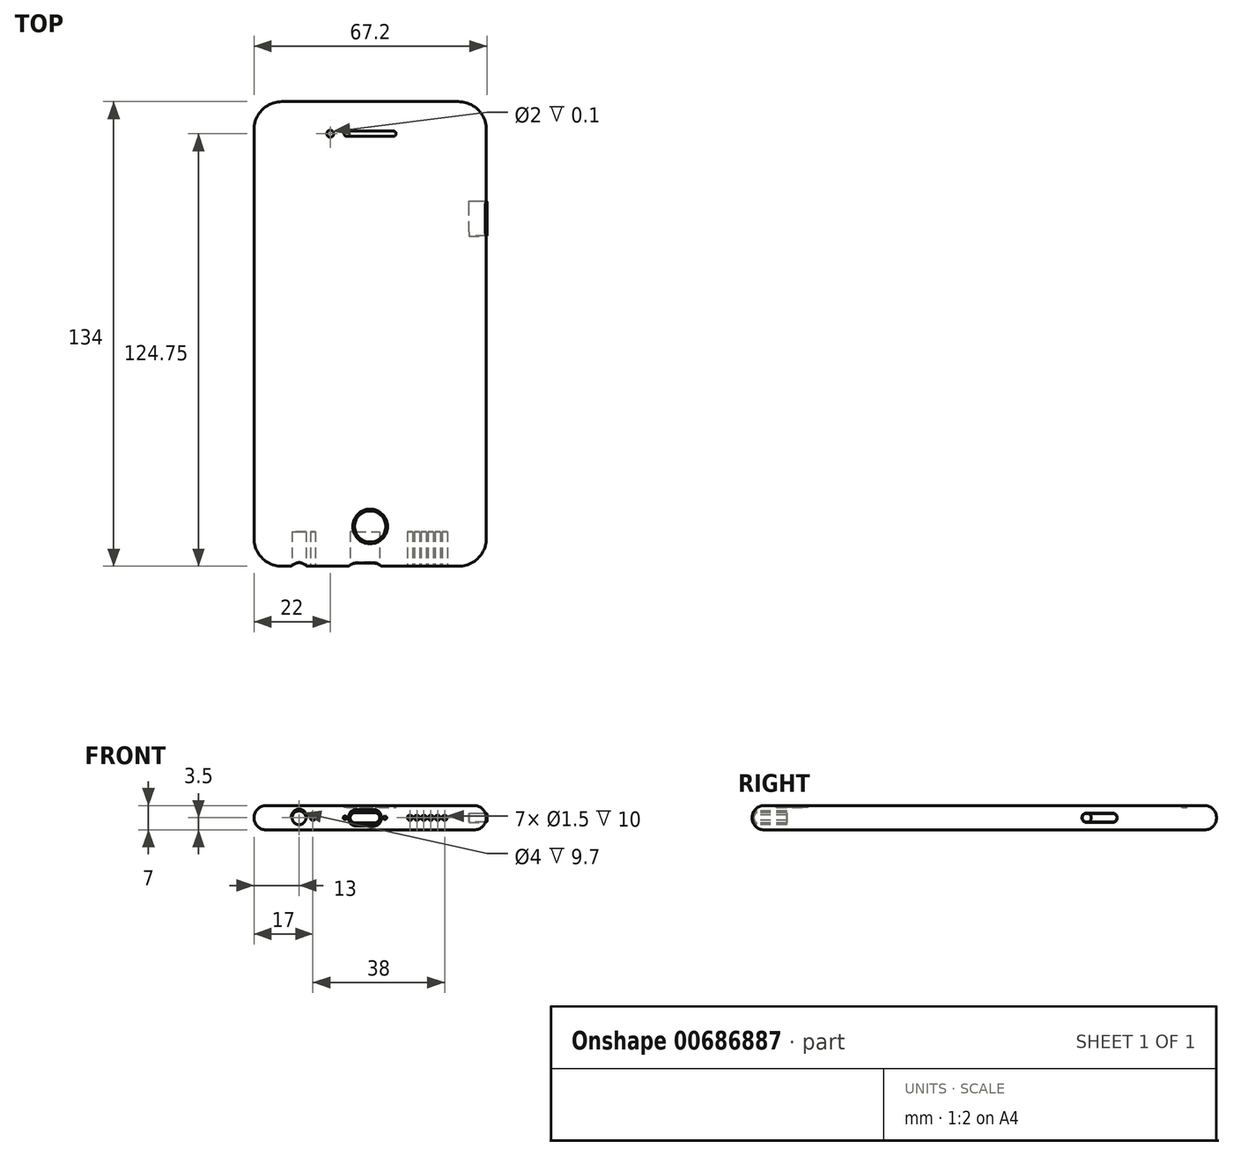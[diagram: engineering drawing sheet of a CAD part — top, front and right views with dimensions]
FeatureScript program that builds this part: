
annotation { "Feature Type Name" : "Feature", "Feature Type Description" : "" }
export const myFeature = defineFeature(function(context is Context, id is Id, definition is map)
    precondition{}
    {
        {
            var Q0;
            Q0=qCreatedBy(makeId("Top.planeOp"),FACE);
            var sketch = newSketch(context, id + "F0", { "sketchPlane" : qUnion([Q0])});
            skLineSegment(sketch, "E0.bottom", {"start": v(0, 0) * mm, "end": v(67, 0) * mm});
            skLineSegment(sketch, "E0.top", {"start": v(0, 134) * mm, "end": v(67, 134) * mm});
            skLineSegment(sketch, "E0.left", {"start": v(0, 0) * mm, "end": v(0, 134) * mm});
            skLineSegment(sketch, "E0.right", {"start": v(67, 0) * mm, "end": v(67, 134) * mm});
            skSolve(sketch);
        }
        {
            var Q0;
            Q0=makeQuery(id+"F0.imprint","IMPRINT",FACE,{"disambiguationData":[TD([[makeQuery(id+"F0.imprint","IMPRINT",EDGE,{"derivedFrom":sQuery(id+"F0.wireOp",EDGE,"E0.bottom")}),1.0]])]});
            extrude(context, id + "F1", {"entities" : qUnion([Q0]), "depth" : 7 * mm, "offsetDistance" : 25 * mm});
        }
        {
            var Q0;
            Q0=makeQuery(id+"F1.opExtrude","SWEPT_EDGE",EDGE,{"disambiguationData":[OSD([sQuery(id+"F0.wireOp",EDGE,"E0.bottom"),sQuery(id+"F0.wireOp",EDGE,"E0.right")])]});
            var Q1;
            Q1=makeQuery(id+"F1.opExtrude","SWEPT_EDGE",EDGE,{"disambiguationData":[OSD([sQuery(id+"F0.wireOp",EDGE,"E0.bottom"),sQuery(id+"F0.wireOp",EDGE,"E0.left")])]});
            var Q2;
            Q2=makeQuery(id+"F1.opExtrude","SWEPT_EDGE",EDGE,{"disambiguationData":[OSD([sQuery(id+"F0.wireOp",EDGE,"E0.top"),sQuery(id+"F0.wireOp",EDGE,"E0.right")])]});
            var Q3;
            Q3=makeQuery(id+"F1.opExtrude","SWEPT_EDGE",EDGE,{"disambiguationData":[OSD([sQuery(id+"F0.wireOp",EDGE,"E0.top"),sQuery(id+"F0.wireOp",EDGE,"E0.left")])]});
            fillet(context, id + "F2", {"entities" : qUnion([Q0, Q1, Q2, Q3]), "radius" : 8 * mm, "tangentPropagation" : true, "allowEdgeOverflow" : false});
        }
        {
            var Q0;
            Q0=makeQuery(id+"F1.opExtrude","SWEPT_FACE",FACE,{"disambiguationData":[OSD([sQuery(id+"F0.wireOp",EDGE,"E0.right")])]});
            var sketch = newSketch(context, id + "F3", { "sketchPlane" : qUnion([Q0])});
            skArc(sketch, "E1", {"start": v(104, 2.25) * mm, "mid": v(105.25, 3.5) * mm, "end": v(104, 4.75) * mm, "construction": true});
            skArc(sketch, "E2", {"start": v(96.5, 4.75) * mm, "mid": v(95.25, 3.5) * mm, "end": v(96.5, 2.25) * mm, "construction": true});
            skLineSegment(sketch, "E3", {"start": v(96.5, 4.75) * mm, "end": v(104, 4.75) * mm, "construction": true});
            skLineSegment(sketch, "E4", {"start": v(96.5, 2.25) * mm, "end": v(104, 2.25) * mm, "construction": true});
            skLineSegment(sketch, "E5", {"start": v(126, 3.5) * mm, "end": v(8, 3.5) * mm, "construction": true});
            skLineSegment(sketch, "E6.0", {"start": v(96.5, 4.85) * mm, "end": v(104, 4.85) * mm});
            skArc(sketch, "E6.1", {"start": v(96.5, 4.85) * mm, "mid": v(95.15, 3.5) * mm, "end": v(96.5, 2.15) * mm});
            skLineSegment(sketch, "E6.2", {"start": v(96.5, 2.15) * mm, "end": v(104, 2.15) * mm});
            skArc(sketch, "E6.3", {"start": v(104, 2.15) * mm, "mid": v(105.35, 3.5) * mm, "end": v(104, 4.85) * mm});
            skSolve(sketch);
        }
        {
            var Q0;
            Q0=makeQuery(id+"F3.imprint","IMPRINT",FACE,{"disambiguationData":[TD([[makeQuery(id+"F3.imprint","IMPRINT",EDGE,{"derivedFrom":sQuery(id+"F3.wireOp",EDGE,"E6.0")}),-1.0]])]});
            extrude(context, id + "F4", {"entities" : qUnion([Q0]), "operationType" : NewBodyOperationType.REMOVE, "oppositeDirection" : true, "depth" : 5 * mm, "offsetDistance" : 25 * mm});
        }
        {
            var Q0;
            Q0=makeQuery(id+"F4.boolean.opBoolean","COPY",FACE,{"derivedFrom":makeQuery(id+"F4.opExtrude","CAP_FACE",FACE,{"disambiguationData":[OSD([sQuery(id+"F3.wireOp",EDGE,"E6.0"),sQuery(id+"F3.wireOp",EDGE,"E6.1"),sQuery(id+"F3.wireOp",EDGE,"E6.2"),sQuery(id+"F3.wireOp",EDGE,"E6.3")])],"isStart":false})});
            var sketch = newSketch(context, id + "F5", { "sketchPlane" : qUnion([Q0])});
            skArc(sketch, "E7", {"start": v(96.5, 4.75) * mm, "mid": v(95.25, 3.5) * mm, "end": v(96.5, 2.25) * mm});
            skArc(sketch, "E8", {"start": v(104, 2.25) * mm, "mid": v(105.25, 3.5) * mm, "end": v(104, 4.75) * mm});
            skLineSegment(sketch, "E9", {"start": v(96.5, 4.75) * mm, "end": v(104, 4.75) * mm});
            skLineSegment(sketch, "E10", {"start": v(96.5, 2.25) * mm, "end": v(104, 2.25) * mm});
            skSolve(sketch);
        }
        {
            var Q0;
            Q0=makeQuery(id+"F5.imprint","IMPRINT",FACE,{"disambiguationData":[TD([[makeQuery(id+"F5.imprint","IMPRINT",EDGE,{"derivedFrom":sQuery(id+"F5.wireOp",EDGE,"E7")}),1.0]])]});
            extrude(context, id + "F6", {"entities" : qUnion([Q0]), "operationType" : NewBodyOperationType.ADD, "depth" : 5.2 * mm, "offsetDistance" : 25 * mm});
        }
        {
            var Q0;
            Q0=makeQuery(id+"F1.opExtrude","SWEPT_FACE",FACE,{"disambiguationData":[OSD([sQuery(id+"F0.wireOp",EDGE,"E0.bottom")])]});
            var sketch = newSketch(context, id + "F7", { "sketchPlane" : qUnion([Q0])});
            skCircle(sketch, "E11", {"center": v(13, 3.5) * mm, "radius": 2 * mm});
            skPoint(sketch, "E11.centerSnap0", {"position": v(8, 3.5) * mm});
            skCircle(sketch, "E12", {"center": v(17, 3.5) * mm, "radius": 0.75 * mm});
            skCircle(sketch, "E13", {"center": v(45, 3.5) * mm, "radius": 0.75 * mm});
            skPoint(sketch, "E13.centerSnap0", {"position": v(59, 3.5) * mm});
            skCircle(sketch, "E14", {"center": v(47, 3.5) * mm, "radius": 0.75 * mm});
            skCircle(sketch, "E15", {"center": v(49, 3.5) * mm, "radius": 0.75 * mm});
            skCircle(sketch, "E16", {"center": v(51, 3.5) * mm, "radius": 0.75 * mm});
            skCircle(sketch, "E17", {"center": v(53, 3.5) * mm, "radius": 0.75 * mm});
            skCircle(sketch, "E18", {"center": v(55, 3.5) * mm, "radius": 0.75 * mm});
            skCircle(sketch, "E19", {"center": v(26.25, 3.5) * mm, "radius": 0.5 * mm});
            skCircle(sketch, "E20", {"center": v(37.75, 3.5) * mm, "radius": 0.5 * mm});
            skArc(sketch, "E21", {"start": v(29.25, 5) * mm, "mid": v(27.75, 3.5) * mm, "end": v(29.25, 2) * mm});
            skArc(sketch, "E22", {"start": v(34.75, 2) * mm, "mid": v(36.25, 3.5) * mm, "end": v(34.75, 5) * mm});
            skLineSegment(sketch, "E23", {"start": v(29.25, 5) * mm, "end": v(34.75, 5) * mm});
            skLineSegment(sketch, "E24", {"start": v(29.25, 2) * mm, "end": v(34.75, 2) * mm});
            skSolve(sketch);
        }
        {
            var Q0;
            Q0=makeQuery(id+"F7.imprint","IMPRINT",FACE,{"disambiguationData":[TD([[makeQuery(id+"F7.imprint","IMPRINT",EDGE,{"derivedFrom":sQuery(id+"F7.wireOp",EDGE,"E18")}),1.0]])]});
            var Q1;
            Q1=makeQuery(id+"F7.imprint","IMPRINT",FACE,{"disambiguationData":[TD([[makeQuery(id+"F7.imprint","IMPRINT",EDGE,{"derivedFrom":sQuery(id+"F7.wireOp",EDGE,"E17")}),1.0]])]});
            var Q2;
            Q2=makeQuery(id+"F7.imprint","IMPRINT",FACE,{"disambiguationData":[TD([[makeQuery(id+"F7.imprint","IMPRINT",EDGE,{"derivedFrom":sQuery(id+"F7.wireOp",EDGE,"E16")}),1.0]])]});
            var Q3;
            Q3=makeQuery(id+"F7.imprint","IMPRINT",FACE,{"disambiguationData":[TD([[makeQuery(id+"F7.imprint","IMPRINT",EDGE,{"derivedFrom":sQuery(id+"F7.wireOp",EDGE,"E15")}),1.0]])]});
            var Q4;
            Q4=makeQuery(id+"F7.imprint","IMPRINT",FACE,{"disambiguationData":[TD([[makeQuery(id+"F7.imprint","IMPRINT",EDGE,{"derivedFrom":sQuery(id+"F7.wireOp",EDGE,"E14")}),1.0]])]});
            var Q5;
            Q5=makeQuery(id+"F7.imprint","IMPRINT",FACE,{"disambiguationData":[TD([[makeQuery(id+"F7.imprint","IMPRINT",EDGE,{"derivedFrom":sQuery(id+"F7.wireOp",EDGE,"E13")}),1.0]])]});
            var Q6;
            Q6=makeQuery(id+"F7.imprint","IMPRINT",FACE,{"disambiguationData":[TD([[makeQuery(id+"F7.imprint","IMPRINT",EDGE,{"derivedFrom":sQuery(id+"F7.wireOp",EDGE,"E21")}),1.0]])]});
            var Q7;
            Q7=makeQuery(id+"F7.imprint","IMPRINT",FACE,{"disambiguationData":[TD([[makeQuery(id+"F7.imprint","IMPRINT",EDGE,{"derivedFrom":sQuery(id+"F7.wireOp",EDGE,"E11")}),1.0]])]});
            var Q8;
            Q8=makeQuery(id+"F7.imprint","IMPRINT",FACE,{"disambiguationData":[TD([[makeQuery(id+"F7.imprint","IMPRINT",EDGE,{"derivedFrom":sQuery(id+"F7.wireOp",EDGE,"E12")}),1.0]])]});
            extrude(context, id + "F8", {"entities" : qUnion([Q0, Q1, Q2, Q3, Q4, Q5, Q6, Q7, Q8]), "operationType" : NewBodyOperationType.REMOVE, "oppositeDirection" : true, "depth" : 10 * mm, "offsetDistance" : 25 * mm});
        }
        {
            var Q0;
            Q0=makeQuery(id+"F7.imprint","IMPRINT",FACE,{"disambiguationData":[TD([[makeQuery(id+"F7.imprint","IMPRINT",EDGE,{"derivedFrom":sQuery(id+"F7.wireOp",EDGE,"E19")}),1.0]])]});
            var Q1;
            Q1=makeQuery(id+"F7.imprint","IMPRINT",FACE,{"disambiguationData":[TD([[makeQuery(id+"F7.imprint","IMPRINT",EDGE,{"derivedFrom":sQuery(id+"F7.wireOp",EDGE,"E20")}),1.0]])]});
            extrude(context, id + "F9", {"entities" : qUnion([Q0, Q1]), "operationType" : NewBodyOperationType.REMOVE, "oppositeDirection" : true, "depth" : 0.2 * mm, "offsetDistance" : 25 * mm});
        }
        {
            var Q0;
            Q0=makeQuery(id+"F1.opExtrude","CAP_EDGE",EDGE,{"disambiguationData":[OSD([sQuery(id+"F0.wireOp",EDGE,"E0.left")])],"isStart":false});
            var Q1;
            Q1=makeQuery(id+"F1.opExtrude","CAP_EDGE",EDGE,{"disambiguationData":[OSD([sQuery(id+"F0.wireOp",EDGE,"E0.left")])],"isStart":true});
            fillet(context, id + "F10", {"entities" : qUnion([Q0, Q1]), "radius" : 3.5 * mm, "tangentPropagation" : true, "allowEdgeOverflow" : false});
        }
        {
            var Q0;
            Q0=makeQuery(id+"F6.opExtrude","CAP_EDGE",EDGE,{"disambiguationData":[OSD([sQuery(id+"F5.wireOp",EDGE,"E9")])],"isStart":false});
            var Q1;
            Q1=makeQuery(id+"F6.opExtrude","CAP_EDGE",EDGE,{"disambiguationData":[OSD([sQuery(id+"F5.wireOp",EDGE,"E7")])],"isStart":false});
            var Q2;
            Q2=makeQuery(id+"F6.opExtrude","CAP_EDGE",EDGE,{"disambiguationData":[OSD([sQuery(id+"F5.wireOp",EDGE,"E10")])],"isStart":false});
            var Q3;
            Q3=makeQuery(id+"F6.opExtrude","CAP_EDGE",EDGE,{"disambiguationData":[OSD([sQuery(id+"F5.wireOp",EDGE,"E8")])],"isStart":false});
            var Q4;
            {var subQ0=sQuery(id+"F0.wireOp",EDGE,"E0.right");Q4=makeQuery(id+"F10.opFillet","BLEND_EDGE",EDGE,{"blendedFrom":[makeQuery(id+"F1.opExtrude","CAP_EDGE",EDGE,{"disambiguationData":[OSD([subQ0])],"isStart":true}),makeQuery(id+"F1.opExtrude","CAP_FACE",FACE,{"disambiguationData":[OSD([sQuery(id+"F0.wireOp",EDGE,"E0.bottom"),sQuery(id+"F0.wireOp",EDGE,"E0.top"),sQuery(id+"F0.wireOp",EDGE,"E0.left"),subQ0])],"isStart":true})],"blendedInto":[makeQuery(id+"F1.opExtrude","CAP_FACE",FACE,{"disambiguationData":[OSD([sQuery(id+"F0.wireOp",EDGE,"E0.bottom"),sQuery(id+"F0.wireOp",EDGE,"E0.top"),sQuery(id+"F0.wireOp",EDGE,"E0.left"),subQ0])],"isStart":true})]});}
            fillet(context, id + "F11", {"entities" : qUnion([Q0, Q1, Q2, Q3, Q4]), "radius" : 0.2 * mm, "tangentPropagation" : true, "allowEdgeOverflow" : false});
        }
        {
            var Q0;
            Q0=makeQuery(id+"F1.opExtrude","CAP_FACE",FACE,{"disambiguationData":[OSD([sQuery(id+"F0.wireOp",EDGE,"E0.bottom"),sQuery(id+"F0.wireOp",EDGE,"E0.top"),sQuery(id+"F0.wireOp",EDGE,"E0.left"),sQuery(id+"F0.wireOp",EDGE,"E0.right")])],"isStart":false});
            var sketch = newSketch(context, id + "F12", { "sketchPlane" : qUnion([Q0])});
            skLineSegment(sketch, "E25.bottom", {"start": v(26, 125.5) * mm, "end": v(41, 125.5) * mm});
            skLineSegment(sketch, "E25.top", {"start": v(26, 124) * mm, "end": v(41, 124) * mm});
            skLineSegment(sketch, "E25.left", {"start": v(26, 125.5) * mm, "end": v(26, 124) * mm});
            skLineSegment(sketch, "E25.right", {"start": v(41, 125.5) * mm, "end": v(41, 124) * mm});
            skSolve(sketch);
        }
        {
            var Q0;
            Q0=makeQuery(id+"F12.imprint","IMPRINT",FACE,{"disambiguationData":[TD([[makeQuery(id+"F12.imprint","IMPRINT",EDGE,{"derivedFrom":sQuery(id+"F12.wireOp",EDGE,"E25.bottom")}),-1.0]])]});
            extrude(context, id + "F13", {"entities" : qUnion([Q0]), "operationType" : NewBodyOperationType.REMOVE, "oppositeDirection" : true, "depth" : 0.5 * mm, "offsetDistance" : 25 * mm});
        }
        {
            var Q0;
            Q0=makeQuery(id+"F13.boolean.opBoolean","COPY",EDGE,{"derivedFrom":makeQuery(id+"F13.opExtrude","SWEPT_EDGE",EDGE,{"disambiguationData":[OSD([sQuery(id+"F12.wireOp",EDGE,"E25.top"),sQuery(id+"F12.wireOp",EDGE,"E25.left")])]})});
            var Q1;
            Q1=makeQuery(id+"F13.boolean.opBoolean","COPY",EDGE,{"derivedFrom":makeQuery(id+"F13.opExtrude","SWEPT_EDGE",EDGE,{"disambiguationData":[OSD([sQuery(id+"F12.wireOp",EDGE,"E25.bottom"),sQuery(id+"F12.wireOp",EDGE,"E25.left")])]})});
            var Q2;
            Q2=makeQuery(id+"F13.boolean.opBoolean","COPY",EDGE,{"derivedFrom":makeQuery(id+"F13.opExtrude","SWEPT_EDGE",EDGE,{"disambiguationData":[OSD([sQuery(id+"F12.wireOp",EDGE,"E25.bottom"),sQuery(id+"F12.wireOp",EDGE,"E25.right")])]})});
            var Q3;
            Q3=makeQuery(id+"F13.boolean.opBoolean","COPY",EDGE,{"derivedFrom":makeQuery(id+"F13.opExtrude","SWEPT_EDGE",EDGE,{"disambiguationData":[OSD([sQuery(id+"F12.wireOp",EDGE,"E25.top"),sQuery(id+"F12.wireOp",EDGE,"E25.right")])]})});
            fillet(context, id + "F14", {"entities" : qUnion([Q0, Q1, Q2, Q3]), "radius" : (1.5 / 2) * mm, "tangentPropagation" : true, "allowEdgeOverflow" : false});
        }
        {
            var Q0;
            Q0=makeQuery(id+"F1.opExtrude","CAP_FACE",FACE,{"disambiguationData":[OSD([sQuery(id+"F0.wireOp",EDGE,"E0.bottom"),sQuery(id+"F0.wireOp",EDGE,"E0.top"),sQuery(id+"F0.wireOp",EDGE,"E0.left"),sQuery(id+"F0.wireOp",EDGE,"E0.right")])],"isStart":false});
            var sketch = newSketch(context, id + "F15", { "sketchPlane" : qUnion([Q0])});
            skCircle(sketch, "E26", {"center": v(33.5, 11.5) * mm, "radius": 5 * mm});
            skPoint(sketch, "E26.centerSnap0", {"position": v(33.5, 3.5) * mm});
            skSolve(sketch);
        }
        {
            var Q0;
            Q0=makeQuery(id+"F15.imprint","IMPRINT",FACE,{"disambiguationData":[TD([[makeQuery(id+"F15.imprint","IMPRINT",EDGE,{"derivedFrom":sQuery(id+"F15.wireOp",EDGE,"E26")}),1.0]])]});
            extrude(context, id + "F16", {"entities" : qUnion([Q0]), "operationType" : NewBodyOperationType.REMOVE, "oppositeDirection" : true, "depth" : 0.5 * mm, "offsetDistance" : 25 * mm});
        }
        {
            var Q0;
            Q0=makeQuery(id+"F16.boolean.opBoolean","COPY",EDGE,{"derivedFrom":makeQuery(id+"F16.opExtrude","CAP_EDGE",EDGE,{"disambiguationData":[OSD([sQuery(id+"F15.wireOp",EDGE,"E26")])],"isStart":false})});
            chamfer(context, id + "F17", {"entities" : qUnion([Q0]), "width" : 0.5 * mm, "tangentPropagation" : true});
        }
        {
            var Q0;
            Q0=makeQuery(id+"F1.opExtrude","CAP_FACE",FACE,{"disambiguationData":[OSD([sQuery(id+"F0.wireOp",EDGE,"E0.bottom"),sQuery(id+"F0.wireOp",EDGE,"E0.top"),sQuery(id+"F0.wireOp",EDGE,"E0.left"),sQuery(id+"F0.wireOp",EDGE,"E0.right")])],"isStart":false});
            var sketch = newSketch(context, id + "F18", { "sketchPlane" : qUnion([Q0])});
            skCircle(sketch, "E27", {"center": v(22, 124.75) * mm, "radius": 1 * mm});
            skSolve(sketch);
        }
        {
            var Q0;
            Q0 = qSketchRegion(id + "F18", true);
            extrude(context, id + "F19", {"entities" : qUnion([Q0]), "operationType" : NewBodyOperationType.REMOVE, "oppositeDirection" : true, "depth" : 0.1 * mm, "offsetDistance" : 25 * mm});
        }
        {
            var Q0;
            Q0=makeQuery(id+"F10.opFillet","BLEND_EDGE",EDGE,{"blendedFrom":[makeQuery(id+"F1.opExtrude","CAP_EDGE",EDGE,{"disambiguationData":[OSD([sQuery(id+"F0.wireOp",EDGE,"E0.bottom")])],"isStart":false}),makeQuery(id+"F8.boolean.opBoolean","COPY",FACE,{"derivedFrom":makeQuery(id+"F8.opExtrude","SWEPT_FACE",FACE,{"disambiguationData":[OSD([sQuery(id+"F7.wireOp",EDGE,"E23")])]})})],"blendedInto":[makeQuery(id+"F8.boolean.opBoolean","COPY",FACE,{"derivedFrom":makeQuery(id+"F8.opExtrude","SWEPT_FACE",FACE,{"disambiguationData":[OSD([sQuery(id+"F7.wireOp",EDGE,"E23")])]})})]});
            var Q1;
            Q1=makeQuery(id+"F10.opFillet","BLEND_EDGE",EDGE,{"blendedFrom":[makeQuery(id+"F1.opExtrude","CAP_EDGE",EDGE,{"disambiguationData":[OSD([sQuery(id+"F0.wireOp",EDGE,"E0.bottom")])],"isStart":true}),makeQuery(id+"F8.boolean.opBoolean","COPY",FACE,{"derivedFrom":makeQuery(id+"F8.opExtrude","SWEPT_FACE",FACE,{"disambiguationData":[OSD([sQuery(id+"F7.wireOp",EDGE,"E24")])]})})],"blendedInto":[makeQuery(id+"F8.boolean.opBoolean","COPY",FACE,{"derivedFrom":makeQuery(id+"F8.opExtrude","SWEPT_FACE",FACE,{"disambiguationData":[OSD([sQuery(id+"F7.wireOp",EDGE,"E24")])]})})]});
            var Q2;
            Q2=makeQuery(id+"F10.opFillet","BLEND_EDGE",EDGE,{"blendedFrom":[makeQuery(id+"F1.opExtrude","CAP_EDGE",EDGE,{"disambiguationData":[OSD([sQuery(id+"F0.wireOp",EDGE,"E0.bottom")])],"isStart":true}),makeQuery(id+"F8.boolean.opBoolean","COPY",FACE,{"derivedFrom":makeQuery(id+"F8.opExtrude","SWEPT_FACE",FACE,{"disambiguationData":[OSD([sQuery(id+"F7.wireOp",EDGE,"E21")])]})})],"blendedInto":[makeQuery(id+"F8.boolean.opBoolean","COPY",FACE,{"derivedFrom":makeQuery(id+"F8.opExtrude","SWEPT_FACE",FACE,{"disambiguationData":[OSD([sQuery(id+"F7.wireOp",EDGE,"E21")])]})})]});
            var Q3;
            Q3=makeQuery(id+"F10.opFillet","BLEND_EDGE",EDGE,{"blendedFrom":[makeQuery(id+"F1.opExtrude","CAP_EDGE",EDGE,{"disambiguationData":[OSD([sQuery(id+"F0.wireOp",EDGE,"E0.bottom")])],"isStart":false}),makeQuery(id+"F8.boolean.opBoolean","COPY",FACE,{"derivedFrom":makeQuery(id+"F8.opExtrude","SWEPT_FACE",FACE,{"disambiguationData":[OSD([sQuery(id+"F7.wireOp",EDGE,"E21")])]})})],"blendedInto":[makeQuery(id+"F8.boolean.opBoolean","COPY",FACE,{"derivedFrom":makeQuery(id+"F8.opExtrude","SWEPT_FACE",FACE,{"disambiguationData":[OSD([sQuery(id+"F7.wireOp",EDGE,"E21")])]})})]});
            var Q4;
            Q4=makeQuery(id+"F10.opFillet","BLEND_EDGE",EDGE,{"blendedFrom":[makeQuery(id+"F1.opExtrude","CAP_EDGE",EDGE,{"disambiguationData":[OSD([sQuery(id+"F0.wireOp",EDGE,"E0.bottom")])],"isStart":true}),makeQuery(id+"F8.boolean.opBoolean","COPY",FACE,{"derivedFrom":makeQuery(id+"F8.opExtrude","SWEPT_FACE",FACE,{"disambiguationData":[OSD([sQuery(id+"F7.wireOp",EDGE,"E22")])]})})],"blendedInto":[makeQuery(id+"F8.boolean.opBoolean","COPY",FACE,{"derivedFrom":makeQuery(id+"F8.opExtrude","SWEPT_FACE",FACE,{"disambiguationData":[OSD([sQuery(id+"F7.wireOp",EDGE,"E22")])]})})]});
            var Q5;
            Q5=makeQuery(id+"F10.opFillet","BLEND_EDGE",EDGE,{"blendedFrom":[makeQuery(id+"F1.opExtrude","CAP_EDGE",EDGE,{"disambiguationData":[OSD([sQuery(id+"F0.wireOp",EDGE,"E0.bottom")])],"isStart":false}),makeQuery(id+"F8.boolean.opBoolean","COPY",FACE,{"derivedFrom":makeQuery(id+"F8.opExtrude","SWEPT_FACE",FACE,{"disambiguationData":[OSD([sQuery(id+"F7.wireOp",EDGE,"E22")])]})})],"blendedInto":[makeQuery(id+"F8.boolean.opBoolean","COPY",FACE,{"derivedFrom":makeQuery(id+"F8.opExtrude","SWEPT_FACE",FACE,{"disambiguationData":[OSD([sQuery(id+"F7.wireOp",EDGE,"E22")])]})})]});
            chamfer(context, id + "F20", {"entities" : qUnion([Q0, Q1, Q2, Q3, Q4, Q5]), "width" : 0.5 * mm});
        }
        {
            var Q0;
            Q0=makeQuery(id+"F10.opFillet","BLEND_EDGE",EDGE,{"blendedFrom":[makeQuery(id+"F1.opExtrude","CAP_EDGE",EDGE,{"disambiguationData":[OSD([sQuery(id+"F0.wireOp",EDGE,"E0.bottom")])],"isStart":true}),makeQuery(id+"F8.boolean.opBoolean","COPY",FACE,{"derivedFrom":makeQuery(id+"F8.opExtrude","SWEPT_FACE",FACE,{"disambiguationData":[OSD([sQuery(id+"F7.wireOp",EDGE,"E11")])]})})],"blendedInto":[makeQuery(id+"F8.boolean.opBoolean","COPY",FACE,{"derivedFrom":makeQuery(id+"F8.opExtrude","SWEPT_FACE",FACE,{"disambiguationData":[OSD([sQuery(id+"F7.wireOp",EDGE,"E11")])]})})]});
            var Q1;
            Q1=makeQuery(id+"F10.opFillet","BLEND_EDGE",EDGE,{"blendedFrom":[makeQuery(id+"F1.opExtrude","CAP_EDGE",EDGE,{"disambiguationData":[OSD([sQuery(id+"F0.wireOp",EDGE,"E0.bottom")])],"isStart":false}),makeQuery(id+"F8.boolean.opBoolean","COPY",FACE,{"derivedFrom":makeQuery(id+"F8.opExtrude","SWEPT_FACE",FACE,{"disambiguationData":[OSD([sQuery(id+"F7.wireOp",EDGE,"E11")])]})})],"blendedInto":[makeQuery(id+"F8.boolean.opBoolean","COPY",FACE,{"derivedFrom":makeQuery(id+"F8.opExtrude","SWEPT_FACE",FACE,{"disambiguationData":[OSD([sQuery(id+"F7.wireOp",EDGE,"E11")])]})})]});
            chamfer(context, id + "F21", {"entities" : qUnion([Q0, Q1]), "width" : 0.3 * mm});
        }
    });
